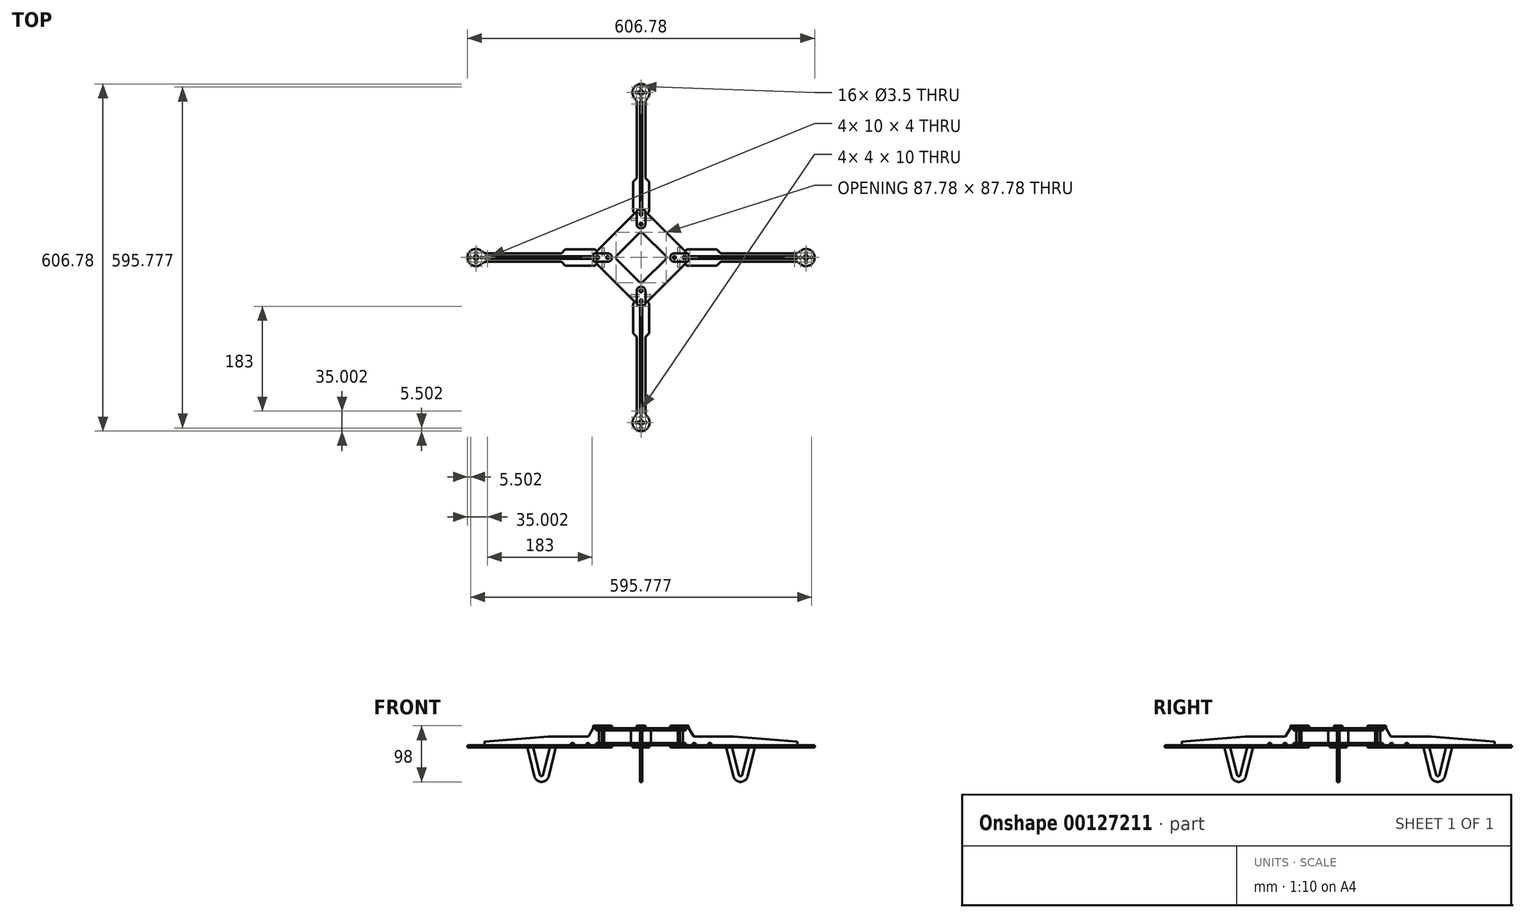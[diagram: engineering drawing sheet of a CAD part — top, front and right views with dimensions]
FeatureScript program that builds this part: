
annotation { "Feature Type Name" : "Feature", "Feature Type Description" : "" }
export const myFeature = defineFeature(function(context is Context, id is Id, definition is map)
    precondition{}
    {
        {
            assignVariable(context, id + "F0", {"name" : "Dicke", "anyValue" : 4 * mm});
        }
        {
            var Q0;
            Q0=qCreatedBy(makeId("Right.planeOp"),FACE);
            var sketch = newSketch(context, id + "F1", { "sketchPlane" : qUnion([Q0])});
            skLineSegment(sketch, "E0", {"start": v(0, 0) * mm, "end": v(0, 100) * mm, "construction": true});
            skSolve(sketch);
        }
        {
            var Q0;
            Q0=qCreatedBy(makeId("Top.planeOp"),FACE);
            var sketch = newSketch(context, id + "F2", { "sketchPlane" : qUnion([Q0])});
            skLineSegment(sketch, "E1.bottom", {"start": v(10, 78.39) * mm, "end": v(2, 78.39) * mm});
            skLineSegment(sketch, "E1.top", {"start": v(10, -78.39) * mm, "end": v(2, -78.39) * mm});
            skLineSegment(sketch, "E1.left", {"start": v(78.39, 10) * mm, "end": v(78.39, 2) * mm});
            skLineSegment(sketch, "E1.right", {"start": v(-78.39, 10) * mm, "end": v(-78.39, 2) * mm});
            skPoint(sketch, "E1.middle", {"position": v(0, 0) * mm});
            skLineSegment(sketch, "E2", {"start": v(-2, -78.39) * mm, "end": v(-2, -73.39) * mm});
            skLineSegment(sketch, "E3", {"start": v(-2, -73.39) * mm, "end": v(2, -73.39) * mm});
            skLineSegment(sketch, "E4", {"start": v(2, -73.39) * mm, "end": v(2, -78.39) * mm});
            skLineSegment(sketch, "E5", {"start": v(-78.39, -2) * mm, "end": v(-73.39, -2) * mm});
            skLineSegment(sketch, "E6", {"start": v(-73.39, -2) * mm, "end": v(-73.39, 2) * mm});
            skLineSegment(sketch, "E7", {"start": v(-73.39, 2) * mm, "end": v(-78.39, 2) * mm});
            skLineSegment(sketch, "E8.MirrorCS", {"start": v(-2, 73.39) * mm, "end": v(2, 73.39) * mm});
            skLineSegment(sketch, "E9.MirrorCS", {"start": v(-2, 78.39) * mm, "end": v(-2, 73.39) * mm});
            skLineSegment(sketch, "E10.MirrorCS", {"start": v(2, 73.39) * mm, "end": v(2, 78.39) * mm});
            skLineSegment(sketch, "E11.MirrorCS", {"start": v(73.39, -2) * mm, "end": v(73.39, 2) * mm});
            skLineSegment(sketch, "E12.MirrorCS", {"start": v(78.39, -2) * mm, "end": v(73.39, -2) * mm});
            skLineSegment(sketch, "E13.MirrorCS", {"start": v(73.39, 2) * mm, "end": v(78.39, 2) * mm});
            skLineSegment(sketch, "E14.trimOffspring", {"start": v(-2, -78.39) * mm, "end": v(-10, -78.39) * mm});
            skLineSegment(sketch, "E15.trimOffspring", {"start": v(-78.39, -2) * mm, "end": v(-78.39, -10) * mm});
            skLineSegment(sketch, "E16.trimOffspring", {"start": v(78.39, -2) * mm, "end": v(78.39, -10) * mm});
            skLineSegment(sketch, "E17.trimOffspring", {"start": v(-2, 78.39) * mm, "end": v(-10, 78.39) * mm});
            skLineSegment(sketch, "E18", {"start": v(-78.39, 10) * mm, "end": v(-10, 78.39) * mm});
            skPoint(sketch, "E19.orphan", {"position": v(-78.39, 78.39) * mm});
            skLineSegment(sketch, "E20.MirrorCS", {"start": v(78.39, 10) * mm, "end": v(10, 78.39) * mm});
            skLineSegment(sketch, "E21.MirrorCS", {"start": v(78.39, -10) * mm, "end": v(10, -78.39) * mm});
            skLineSegment(sketch, "E22.MirrorCS", {"start": v(-78.39, -10) * mm, "end": v(-10, -78.39) * mm});
            skPoint(sketch, "E23.orphan", {"position": v(-78.39, -78.39) * mm});
            skPoint(sketch, "E24.orphan", {"position": v(78.39, -78.39) * mm});
            skPoint(sketch, "E25.orphan", {"position": v(78.39, 78.39) * mm});
            skSolve(sketch);
        }
        {
            var Q0;
            Q0 = qSketchRegion(id + "F2", true);
            extrude(context, id + "F3", {"entities" : qUnion([Q0]), "depth" : getVariable(context, 'Dicke')});
        }
        {
            var Q0;
            Q0=qCreatedBy(makeId("Top.planeOp"),FACE);
            cPlane(context, id + "F4", {"entities" : qUnion([Q0]), "cplaneType" : CPlaneType.OFFSET, "offset" : 30 * mm, "width" : 150 * mm, "height" : 150 * mm});
        }
        {
            var Q0;
            Q0=makeQuery(id+"F3.opExtrude","SWEPT_BODY",BODY,{"disambiguationData":[OSD([sQuery(id+"F2.wireOp",EDGE,"E1.bottom"),sQuery(id+"F2.wireOp",EDGE,"E1.top"),sQuery(id+"F2.wireOp",EDGE,"E1.left"),sQuery(id+"F2.wireOp",EDGE,"E1.right"),sQuery(id+"F2.wireOp",EDGE,"E2"),sQuery(id+"F2.wireOp",EDGE,"E3"),sQuery(id+"F2.wireOp",EDGE,"E4"),sQuery(id+"F2.wireOp",EDGE,"E5"),sQuery(id+"F2.wireOp",EDGE,"E6"),sQuery(id+"F2.wireOp",EDGE,"E7"),sQuery(id+"F2.wireOp",EDGE,"E8.MirrorCS"),sQuery(id+"F2.wireOp",EDGE,"E9.MirrorCS"),sQuery(id+"F2.wireOp",EDGE,"E10.MirrorCS"),sQuery(id+"F2.wireOp",EDGE,"E11.MirrorCS"),sQuery(id+"F2.wireOp",EDGE,"E12.MirrorCS"),sQuery(id+"F2.wireOp",EDGE,"E13.MirrorCS"),sQuery(id+"F2.wireOp",EDGE,"E14.trimOffspring"),sQuery(id+"F2.wireOp",EDGE,"E15.trimOffspring"),sQuery(id+"F2.wireOp",EDGE,"E16.trimOffspring"),sQuery(id+"F2.wireOp",EDGE,"E17.trimOffspring"),sQuery(id+"F2.wireOp",EDGE,"E18"),sQuery(id+"F2.wireOp",EDGE,"E20.MirrorCS"),sQuery(id+"F2.wireOp",EDGE,"E21.MirrorCS"),sQuery(id+"F2.wireOp",EDGE,"E22.MirrorCS")])]});
            transform(context, id + "F5", {"entities" : qUnion([Q0]), "transformType" : TransformType.TRANSLATION_3D, "dx" : 0 * mm, "dy" : 0 * mm, "dz" : 26 * mm, "makeCopy" : true});
        }
        {
            var Q0;
            Q0=makeQuery(id+"F5.opPattern","COPY",FACE,{"derivedFrom":makeQuery(id+"F3.opExtrude","CAP_FACE",FACE,{"disambiguationData":[OSD([sQuery(id+"F2.wireOp",EDGE,"E1.bottom"),sQuery(id+"F2.wireOp",EDGE,"E1.top"),sQuery(id+"F2.wireOp",EDGE,"E1.left"),sQuery(id+"F2.wireOp",EDGE,"E1.right"),sQuery(id+"F2.wireOp",EDGE,"E2"),sQuery(id+"F2.wireOp",EDGE,"E3"),sQuery(id+"F2.wireOp",EDGE,"E4"),sQuery(id+"F2.wireOp",EDGE,"E5"),sQuery(id+"F2.wireOp",EDGE,"E6"),sQuery(id+"F2.wireOp",EDGE,"E7"),sQuery(id+"F2.wireOp",EDGE,"E8.MirrorCS"),sQuery(id+"F2.wireOp",EDGE,"E9.MirrorCS"),sQuery(id+"F2.wireOp",EDGE,"E10.MirrorCS"),sQuery(id+"F2.wireOp",EDGE,"E11.MirrorCS"),sQuery(id+"F2.wireOp",EDGE,"E12.MirrorCS"),sQuery(id+"F2.wireOp",EDGE,"E13.MirrorCS"),sQuery(id+"F2.wireOp",EDGE,"E14.trimOffspring"),sQuery(id+"F2.wireOp",EDGE,"E15.trimOffspring"),sQuery(id+"F2.wireOp",EDGE,"E16.trimOffspring"),sQuery(id+"F2.wireOp",EDGE,"E17.trimOffspring"),sQuery(id+"F2.wireOp",EDGE,"E18"),sQuery(id+"F2.wireOp",EDGE,"E20.MirrorCS"),sQuery(id+"F2.wireOp",EDGE,"E21.MirrorCS"),sQuery(id+"F2.wireOp",EDGE,"E22.MirrorCS")])],"isStart":false}),"instanceName":"1"});
            var sketch = newSketch(context, id + "F6", { "sketchPlane" : qUnion([Q0])});
            skLineSegment(sketch, "E26", {"start": v(0, -45.96) * mm, "end": v(45.96, 0) * mm});
            skLineSegment(sketch, "E27", {"start": v(45.96, 0) * mm, "end": v(0, 45.96) * mm});
            skLineSegment(sketch, "E28", {"start": v(0, 45.96) * mm, "end": v(-45.96, 0) * mm});
            skLineSegment(sketch, "E29", {"start": v(-45.96, 0) * mm, "end": v(0, -45.96) * mm});
            skSolve(sketch);
        }
        {
            var Q0;
            Q0 = qSketchRegion(id + "F6", true);
            extrude(context, id + "F7", {"entities" : qUnion([Q0]), "operationType" : NewBodyOperationType.REMOVE, "oppositeDirection" : true, "depth" : 25 * mm});
        }
        {
            var Q0;
            Q0=makeQuery(id+"F7.boolean.opBoolean","COPY",EDGE,{"derivedFrom":makeQuery(id+"F7.opExtrude","SWEPT_EDGE",EDGE,{"disambiguationData":[OSD([sQuery(id+"F6.wireOp",EDGE,"E26"),sQuery(id+"F6.wireOp",EDGE,"E29")])]})});
            var Q1;
            Q1=makeQuery(id+"F7.boolean.opBoolean","COPY",EDGE,{"derivedFrom":makeQuery(id+"F7.opExtrude","SWEPT_EDGE",EDGE,{"disambiguationData":[OSD([sQuery(id+"F6.wireOp",EDGE,"E28"),sQuery(id+"F6.wireOp",EDGE,"E29")])]})});
            var Q2;
            Q2=makeQuery(id+"F7.boolean.opBoolean","COPY",EDGE,{"derivedFrom":makeQuery(id+"F7.opExtrude","SWEPT_EDGE",EDGE,{"disambiguationData":[OSD([sQuery(id+"F6.wireOp",EDGE,"E27"),sQuery(id+"F6.wireOp",EDGE,"E28")])]})});
            var Q3;
            Q3=makeQuery(id+"F7.boolean.opBoolean","COPY",EDGE,{"derivedFrom":makeQuery(id+"F7.opExtrude","SWEPT_EDGE",EDGE,{"disambiguationData":[OSD([sQuery(id+"F6.wireOp",EDGE,"E26"),sQuery(id+"F6.wireOp",EDGE,"E27")])]})});
            fillet(context, id + "F8", {"entities" : qUnion([Q0, Q1, Q2, Q3]), "radius" : 5 * mm, "tangentPropagation" : true, "allowEdgeOverflow" : false});
        }
        {
            var Q0;
            Q0=qCreatedBy(makeId("Top.planeOp"),FACE);
            var sketch = newSketch(context, id + "F9", { "sketchPlane" : qUnion([Q0])});
            skArc(sketch, "E30", {"start": v(10.5, 277.68) * mm, "mid": v(0, 303.39) * mm, "end": v(-10.5, 277.68) * mm});
            skLineSegment(sketch, "E31", {"start": v(-7.5, 270.53) * mm, "end": v(-7.5, 138.89) * mm});
            skArc(sketch, "E32", {"start": v(-7.5, 58.39) * mm, "mid": v(0, 50.89) * mm, "end": v(7.5, 58.39) * mm});
            skLineSegment(sketch, "E33", {"start": v(7.5, 58.39) * mm, "end": v(7.5, 73.89) * mm});
            skPoint(sketch, "E34.visualSharp", {"position": v(7.5, 275.4) * mm});
            skArc(sketch, "E34.filletArc", {"start": v(10.5, 277.68) * mm, "mid": v(8.28, 274.4) * mm, "end": v(7.5, 270.53) * mm});
            skPoint(sketch, "E35.visualSharp", {"position": v(-7.5, 275.4) * mm});
            skArc(sketch, "E35.filletArc", {"start": v(-7.5, 270.53) * mm, "mid": v(-8.28, 274.4) * mm, "end": v(-10.5, 277.68) * mm});
            skPoint(sketch, "E36", {"position": v(0, 303.39) * mm});
            skLineSegment(sketch, "E37", {"start": v(0, 278.89) * mm, "end": v(0, 297.89) * mm, "construction": true});
            skLineSegment(sketch, "E38", {"start": v(-8, 288.39) * mm, "end": v(8, 288.39) * mm, "construction": true});
            skCircle(sketch, "E39", {"center": v(-8, 288.39) * mm, "radius": 1.75 * mm});
            skCircle(sketch, "E40", {"center": v(0, 297.89) * mm, "radius": 1.75 * mm});
            skCircle(sketch, "E41", {"center": v(8, 288.39) * mm, "radius": 1.75 * mm});
            skCircle(sketch, "E42", {"center": v(0, 278.89) * mm, "radius": 1.75 * mm});
            skCircle(sketch, "E43", {"center": v(0, 58.39) * mm, "radius": 2.5 * mm});
            skLineSegment(sketch, "E44", {"start": v(7.5, 73.89) * mm, "end": v(14, 80.39) * mm});
            skLineSegment(sketch, "E45", {"start": v(14, 80.39) * mm, "end": v(14, 132.39) * mm});
            skLineSegment(sketch, "E46", {"start": v(14, 132.39) * mm, "end": v(7.5, 138.89) * mm});
            skLineSegment(sketch, "E47.MirrorCS", {"start": v(-7.5, 73.89) * mm, "end": v(-14, 80.39) * mm});
            skLineSegment(sketch, "E48.MirrorCS", {"start": v(-14, 80.39) * mm, "end": v(-14, 132.39) * mm});
            skLineSegment(sketch, "E49.MirrorCS", {"start": v(-14, 132.39) * mm, "end": v(-7.5, 138.89) * mm});
            skLineSegment(sketch, "E50.trimOffspring", {"start": v(7.5, 138.89) * mm, "end": v(7.5, 270.53) * mm});
            skLineSegment(sketch, "E51.trimOffspring", {"start": v(-7.5, 73.89) * mm, "end": v(-7.5, 58.39) * mm});
            skLineSegment(sketch, "E52", {"start": v(7.5, 73.89) * mm, "end": v(-7.5, 73.89) * mm, "construction": true});
            skCircle(sketch, "E53", {"center": v(0, 288.39) * mm, "radius": 4 * mm});
            skSolve(sketch);
        }
        {
            var Q0;
            Q0=qCreatedBy(makeId("Top.planeOp"),FACE);
            var sketch = newSketch(context, id + "F10", { "sketchPlane" : qUnion([Q0])});
            skCircle(sketch, "E54", {"center": v(0, 288.39) * mm, "radius": 14 * mm});
            skCircle(sketch, "E55", {"center": v(0, 288.39) * mm, "radius": 127 * mm});
            skSolve(sketch);
        }
        {
            var Q0;
            Q0 = qSketchRegion(id + "F9", true);
            extrude(context, id + "F11", {"entities" : qUnion([Q0]), "oppositeDirection" : true, "depth" : getVariable(context, 'Dicke')});
        }
        {
            var Q0;
            Q0=qCreatedBy(makeId("Right.planeOp"),FACE);
            var sketch = newSketch(context, id + "F12", { "sketchPlane" : qUnion([Q0])});
            skLineSegment(sketch, "E56", {"start": v(92.05, 15) * mm, "end": v(162.05, 15) * mm});
            skLineSegment(sketch, "E57", {"start": v(162.05, 15) * mm, "end": v(273.39, 6) * mm});
            skLineSegment(sketch, "E58", {"start": v(273.39, 6) * mm, "end": v(273.39, -4) * mm});
            skLineSegment(sketch, "E59", {"start": v(263.39, 0) * mm, "end": v(122.39, 0) * mm});
            skLineSegment(sketch, "E60", {"start": v(73.39, 0) * mm, "end": v(73.39, 34) * mm});
            skLineSegment(sketch, "E61.top", {"start": v(90.39, 4) * mm, "end": v(95.39, 4) * mm});
            skLineSegment(sketch, "E61.left", {"start": v(90.39, -4) * mm, "end": v(90.39, 4) * mm});
            skLineSegment(sketch, "E61.right", {"start": v(95.39, 0) * mm, "end": v(95.39, 4) * mm});
            skLineSegment(sketch, "E62.top", {"start": v(122.39, 4) * mm, "end": v(117.39, 4) * mm});
            skLineSegment(sketch, "E62.left", {"start": v(122.39, 0) * mm, "end": v(122.39, 4) * mm});
            skLineSegment(sketch, "E62.right", {"start": v(117.39, 0) * mm, "end": v(117.39, 4) * mm});
            skLineSegment(sketch, "E63.trimOffspring", {"start": v(80.39, 0) * mm, "end": v(73.39, 0) * mm});
            skLineSegment(sketch, "E64.trimOffspring", {"start": v(117.39, 0) * mm, "end": v(95.39, 0) * mm});
            skLineSegment(sketch, "E65", {"start": v(92.05, 15) * mm, "end": v(83.39, 30) * mm});
            skLineSegment(sketch, "E66", {"start": v(83.39, 30) * mm, "end": v(78.39, 30) * mm});
            skLineSegment(sketch, "E67", {"start": v(78.39, 30) * mm, "end": v(78.39, 34) * mm});
            skLineSegment(sketch, "E68", {"start": v(78.39, 34) * mm, "end": v(73.39, 34) * mm});
            skLineSegment(sketch, "E69", {"start": v(80.39, 0) * mm, "end": v(80.39, -4) * mm});
            skLineSegment(sketch, "E70", {"start": v(80.39, -4) * mm, "end": v(90.39, -4) * mm});
            skLineSegment(sketch, "E71", {"start": v(263.39, 0) * mm, "end": v(263.39, -4) * mm});
            skLineSegment(sketch, "E72", {"start": v(263.39, -4) * mm, "end": v(273.39, -4) * mm});
            skSolve(sketch);
        }
        {
            var Q0;
            Q0 = qSketchRegion(id + "F12", true);
            extrude(context, id + "F13", {"entities" : qUnion([Q0]), "endBound" : BoundingType.SYMMETRIC, "depth" : getVariable(context, 'Dicke')});
        }
        {
            var Q0;
            Q0=qCreatedBy(makeId("Right.planeOp"),FACE);
            var sketch = newSketch(context, id + "F14", { "sketchPlane" : qUnion([Q0])});
            skLineSegment(sketch, "E73", {"start": v(148.89, -4) * mm, "end": v(161.27, -54.12) * mm});
            skArc(sketch, "E74", {"start": v(161.27, -54.12) * mm, "mid": v(173.89, -64) * mm, "end": v(186.5, -54.12) * mm});
            skLineSegment(sketch, "E75", {"start": v(186.5, -54.12) * mm, "end": v(198.89, -4) * mm});
            skLineSegment(sketch, "E76.0", {"start": v(176.8, -51.72) * mm, "end": v(188.59, -4) * mm});
            skArc(sketch, "E76.1", {"start": v(170.98, -51.72) * mm, "mid": v(173.89, -54) * mm, "end": v(176.8, -51.72) * mm});
            skLineSegment(sketch, "E76.2", {"start": v(159.19, -4) * mm, "end": v(170.98, -51.72) * mm});
            skLineSegment(sketch, "E77", {"start": v(148.89, -4) * mm, "end": v(154.19, -4) * mm});
            skLineSegment(sketch, "E78", {"start": v(154.19, -4) * mm, "end": v(154.19, 0) * mm});
            skLineSegment(sketch, "E79", {"start": v(154.19, 0) * mm, "end": v(159.19, 0) * mm});
            skLineSegment(sketch, "E80", {"start": v(159.19, 0) * mm, "end": v(159.19, -4) * mm});
            skLineSegment(sketch, "E81", {"start": v(188.59, -4) * mm, "end": v(188.59, 0) * mm});
            skLineSegment(sketch, "E82", {"start": v(188.59, 0) * mm, "end": v(193.59, 0) * mm});
            skLineSegment(sketch, "E83", {"start": v(193.59, 0) * mm, "end": v(193.59, -4) * mm});
            skLineSegment(sketch, "E84", {"start": v(193.59, -4) * mm, "end": v(198.89, -4) * mm});
            skSolve(sketch);
        }
        {
            var Q0;
            Q0 = qSketchRegion(id + "F14", true);
            extrude(context, id + "F15", {"entities" : qUnion([Q0]), "endBound" : BoundingType.SYMMETRIC, "depth" : getVariable(context, 'Dicke')});
        }
        {
            var Q0;
            Q0=qCreatedBy(id+"F4.planeOp",FACE);
            var sketch = newSketch(context, id + "F16", { "sketchPlane" : qUnion([Q0])});
            skLineSegment(sketch, "E85.0", {"start": v(-7.5, 73.89) * mm, "end": v(-7.5, 58.39) * mm});
            skArc(sketch, "E86.0", {"start": v(-7.5, 58.39) * mm, "mid": v(0, 50.89) * mm, "end": v(7.5, 58.39) * mm});
            skLineSegment(sketch, "E87.0", {"start": v(7.5, 58.39) * mm, "end": v(7.5, 73.89) * mm});
            skCircle(sketch, "E88.0", {"center": v(0, 58.39) * mm, "radius": 2.5 * mm});
            skLineSegment(sketch, "E89", {"start": v(-7.5, 73.89) * mm, "end": v(-7.5, 80.39) * mm});
            skLineSegment(sketch, "E90", {"start": v(7.5, 73.89) * mm, "end": v(7.5, 80.39) * mm});
            skLineSegment(sketch, "E91", {"start": v(-4.5, 83.39) * mm, "end": v(4.5, 83.39) * mm});
            skPoint(sketch, "E92.visualSharp", {"position": v(-7.5, 83.39) * mm});
            skArc(sketch, "E92.filletArc", {"start": v(-4.5, 83.39) * mm, "mid": v(-6.62, 82.5) * mm, "end": v(-7.5, 80.39) * mm});
            skPoint(sketch, "E93.visualSharp", {"position": v(7.5, 83.39) * mm});
            skArc(sketch, "E93.filletArc", {"start": v(7.5, 80.39) * mm, "mid": v(6.62, 82.5) * mm, "end": v(4.5, 83.39) * mm});
            skSolve(sketch);
        }
        {
            var Q0;
            Q0 = qSketchRegion(id + "F16", true);
            extrude(context, id + "F17", {"entities" : qUnion([Q0]), "depth" : getVariable(context, 'Dicke')});
        }
        {
            var Q0;
            Q0=makeQuery(id+"F13.opExtrude","SWEPT_BODY",BODY,{"disambiguationData":[OSD([sQuery(id+"F12.wireOp",EDGE,"E56"),sQuery(id+"F12.wireOp",EDGE,"E57"),sQuery(id+"F12.wireOp",EDGE,"E58"),sQuery(id+"F12.wireOp",EDGE,"E59"),sQuery(id+"F12.wireOp",EDGE,"E60"),sQuery(id+"F12.wireOp",EDGE,"E61.top"),sQuery(id+"F12.wireOp",EDGE,"E61.left"),sQuery(id+"F12.wireOp",EDGE,"E61.right"),sQuery(id+"F12.wireOp",EDGE,"E62.top"),sQuery(id+"F12.wireOp",EDGE,"E62.left"),sQuery(id+"F12.wireOp",EDGE,"E62.right"),sQuery(id+"F12.wireOp",EDGE,"E63.trimOffspring"),sQuery(id+"F12.wireOp",EDGE,"E64.trimOffspring"),sQuery(id+"F12.wireOp",EDGE,"E65"),sQuery(id+"F12.wireOp",EDGE,"E66"),sQuery(id+"F12.wireOp",EDGE,"E67"),sQuery(id+"F12.wireOp",EDGE,"E68")])]});
            var Q1;
            Q1=makeQuery(id+"F17.opExtrude","SWEPT_BODY",BODY,{"disambiguationData":[OSD([sQuery(id+"F16.wireOp",EDGE,"E85.0"),sQuery(id+"F16.wireOp",EDGE,"E86.0"),sQuery(id+"F16.wireOp",EDGE,"E87.0"),sQuery(id+"F16.wireOp",EDGE,"E88.0"),sQuery(id+"F16.wireOp",EDGE,"E89"),sQuery(id+"F16.wireOp",EDGE,"E90"),sQuery(id+"F16.wireOp",EDGE,"E91"),sQuery(id+"F16.wireOp",EDGE,"E92.filletArc"),sQuery(id+"F16.wireOp",EDGE,"E93.filletArc")])]});
            var Q2;
            Q2=makeQuery(id+"F3.opExtrude","SWEPT_BODY",BODY,{"disambiguationData":[OSD([sQuery(id+"F2.wireOp",EDGE,"E1.bottom"),sQuery(id+"F2.wireOp",EDGE,"E1.top"),sQuery(id+"F2.wireOp",EDGE,"E1.left"),sQuery(id+"F2.wireOp",EDGE,"E1.right")])]});
            var Q3;
            Q3=makeQuery(id+"FhrMNaqe6fnIL6q_1.opExtrude","SWEPT_BODY",BODY,{"disambiguationData":[OSD([sQuery(id+"FcWjo9COieUKBjw_1.wireOp",EDGE,"a90fca38-8a13-4d0b-956b-f1cffcdc3152.0"),sQuery(id+"FcWjo9COieUKBjw_1.wireOp",EDGE,"fbc8aa7a-db77-4349-b2f0-69285a5e3160.0"),sQuery(id+"FcWjo9COieUKBjw_1.wireOp",EDGE,"03366df2-630f-4610-a856-3e1fcb18efef.0"),sQuery(id+"FcWjo9COieUKBjw_1.wireOp",EDGE,"1a7c9859-e6ac-4236-bc2e-86e582c79c75.0"),sQuery(id+"FcWjo9COieUKBjw_1.wireOp",EDGE,"497b7f40-1a27-446f-bee7-4e00cf973d28.0"),sQuery(id+"FcWjo9COieUKBjw_1.wireOp",EDGE,"497b7f40-1a27-446f-bee7-4e00cf973d28.1"),sQuery(id+"FcWjo9COieUKBjw_1.wireOp",EDGE,"497b7f40-1a27-446f-bee7-4e00cf973d28.2"),sQuery(id+"FcWjo9COieUKBjw_1.wireOp",EDGE,"497b7f40-1a27-446f-bee7-4e00cf973d28.3")])]});
            booleanBodies(context, id + "F18", {"operationType" : BooleanOperationType.SUBTRACTION, "tools" : qUnion([Q0]), "targets" : qUnion([Q1, Q2, Q3]), "keepTools" : true});
        }
        {
            var Q0;
            Q0=makeQuery(id+"F13.opExtrude","SWEPT_BODY",BODY,{"disambiguationData":[OSD([sQuery(id+"F12.wireOp",EDGE,"E56"),sQuery(id+"F12.wireOp",EDGE,"E57"),sQuery(id+"F12.wireOp",EDGE,"E58"),sQuery(id+"F12.wireOp",EDGE,"E59"),sQuery(id+"F12.wireOp",EDGE,"E60"),sQuery(id+"F12.wireOp",EDGE,"E61.top"),sQuery(id+"F12.wireOp",EDGE,"E61.left"),sQuery(id+"F12.wireOp",EDGE,"E61.right"),sQuery(id+"F12.wireOp",EDGE,"E62.top"),sQuery(id+"F12.wireOp",EDGE,"E62.left"),sQuery(id+"F12.wireOp",EDGE,"E62.right"),sQuery(id+"F12.wireOp",EDGE,"E63.trimOffspring"),sQuery(id+"F12.wireOp",EDGE,"E64.trimOffspring"),sQuery(id+"F12.wireOp",EDGE,"E65"),sQuery(id+"F12.wireOp",EDGE,"E66"),sQuery(id+"F12.wireOp",EDGE,"E67"),sQuery(id+"F12.wireOp",EDGE,"E68"),sQuery(id+"F12.wireOp",EDGE,"E69"),sQuery(id+"F12.wireOp",EDGE,"E70"),sQuery(id+"F12.wireOp",EDGE,"E71"),sQuery(id+"F12.wireOp",EDGE,"E72")])]});
            var Q1;
            Q1=makeQuery(id+"F15.opExtrude","SWEPT_BODY",BODY,{"disambiguationData":[OSD([sQuery(id+"F14.wireOp",EDGE,"E73"),sQuery(id+"F14.wireOp",EDGE,"E74"),sQuery(id+"F14.wireOp",EDGE,"E75"),sQuery(id+"F14.wireOp",EDGE,"E76.0"),sQuery(id+"F14.wireOp",EDGE,"E76.1"),sQuery(id+"F14.wireOp",EDGE,"E76.2"),sQuery(id+"F14.wireOp",EDGE,"E77"),sQuery(id+"F14.wireOp",EDGE,"E78"),sQuery(id+"F14.wireOp",EDGE,"E79"),sQuery(id+"F14.wireOp",EDGE,"E80"),sQuery(id+"F14.wireOp",EDGE,"E81"),sQuery(id+"F14.wireOp",EDGE,"E82"),sQuery(id+"F14.wireOp",EDGE,"E83"),sQuery(id+"F14.wireOp",EDGE,"E84")])]});
            var Q2;
            Q2=makeQuery(id+"F11.opExtrude","SWEPT_BODY",BODY,{"disambiguationData":[OSD([sQuery(id+"F9.wireOp",EDGE,"E30"),sQuery(id+"F9.wireOp",EDGE,"E31"),sQuery(id+"F9.wireOp",EDGE,"E32"),sQuery(id+"F9.wireOp",EDGE,"E33"),sQuery(id+"F9.wireOp",EDGE,"E34.filletArc"),sQuery(id+"F9.wireOp",EDGE,"E35.filletArc"),sQuery(id+"F9.wireOp",EDGE,"E39"),sQuery(id+"F9.wireOp",EDGE,"E40"),sQuery(id+"F9.wireOp",EDGE,"E41"),sQuery(id+"F9.wireOp",EDGE,"E42"),sQuery(id+"F9.wireOp",EDGE,"E43"),sQuery(id+"F9.wireOp",EDGE,"E44"),sQuery(id+"F9.wireOp",EDGE,"E45"),sQuery(id+"F9.wireOp",EDGE,"E46"),sQuery(id+"F9.wireOp",EDGE,"E47.MirrorCS"),sQuery(id+"F9.wireOp",EDGE,"E48.MirrorCS"),sQuery(id+"F9.wireOp",EDGE,"E49.MirrorCS"),sQuery(id+"F9.wireOp",EDGE,"E50.trimOffspring"),sQuery(id+"F9.wireOp",EDGE,"E51.trimOffspring")])]});
            booleanBodies(context, id + "F19", {"operationType" : BooleanOperationType.SUBTRACTION, "tools" : qUnion([Q0, Q1]), "targets" : qUnion([Q2]), "keepTools" : true});
        }
        {
            var Q0;
            Q0=makeQuery(id+"F3.opExtrude","CAP_FACE",FACE,{"disambiguationData":[OSD([sQuery(id+"F2.wireOp",EDGE,"E1.bottom"),sQuery(id+"F2.wireOp",EDGE,"E1.top"),sQuery(id+"F2.wireOp",EDGE,"E1.left"),sQuery(id+"F2.wireOp",EDGE,"E1.right"),sQuery(id+"F2.wireOp",EDGE,"E2"),sQuery(id+"F2.wireOp",EDGE,"E3"),sQuery(id+"F2.wireOp",EDGE,"E4"),sQuery(id+"F2.wireOp",EDGE,"E5"),sQuery(id+"F2.wireOp",EDGE,"E6"),sQuery(id+"F2.wireOp",EDGE,"E7"),sQuery(id+"F2.wireOp",EDGE,"E8.MirrorCS"),sQuery(id+"F2.wireOp",EDGE,"E9.MirrorCS"),sQuery(id+"F2.wireOp",EDGE,"E10.MirrorCS"),sQuery(id+"F2.wireOp",EDGE,"E11.MirrorCS"),sQuery(id+"F2.wireOp",EDGE,"E12.MirrorCS"),sQuery(id+"F2.wireOp",EDGE,"E13.MirrorCS"),sQuery(id+"F2.wireOp",EDGE,"E14.trimOffspring"),sQuery(id+"F2.wireOp",EDGE,"E15.trimOffspring"),sQuery(id+"F2.wireOp",EDGE,"E16.trimOffspring"),sQuery(id+"F2.wireOp",EDGE,"E17.trimOffspring"),sQuery(id+"F2.wireOp",EDGE,"E18"),sQuery(id+"F2.wireOp",EDGE,"E20.MirrorCS"),sQuery(id+"F2.wireOp",EDGE,"E21.MirrorCS"),sQuery(id+"F2.wireOp",EDGE,"E22.MirrorCS")])],"isStart":false});
            var sketch = newSketch(context, id + "F20", { "sketchPlane" : qUnion([Q0])});
            skLineSegment(sketch, "E94.bottom", {"start": v(17.5, 68.39) * mm, "end": v(-17.5, 68.39) * mm});
            skLineSegment(sketch, "E94.top", {"start": v(17.5, 64.39) * mm, "end": v(-17.5, 64.39) * mm});
            skLineSegment(sketch, "E94.left", {"start": v(17.5, 68.39) * mm, "end": v(17.5, 64.39) * mm});
            skLineSegment(sketch, "E94.right", {"start": v(-17.5, 68.39) * mm, "end": v(-17.5, 64.39) * mm});
            skSolve(sketch);
        }
        {
            var Q0;
            Q0 = qSketchRegion(id + "F20", true);
            extrude(context, id + "F21", {"entities" : qUnion([Q0]), "endBound" : BoundingType.UP_TO_NEXT, "depth" : 25 * mm});
        }
        {
            var Q0;
            Q0=makeQuery(id+"F17.opExtrude","SWEPT_BODY",BODY,{"disambiguationData":[OSD([sQuery(id+"F16.wireOp",EDGE,"E85.0"),sQuery(id+"F16.wireOp",EDGE,"E86.0"),sQuery(id+"F16.wireOp",EDGE,"E87.0"),sQuery(id+"F16.wireOp",EDGE,"E88.0"),sQuery(id+"F16.wireOp",EDGE,"E89"),sQuery(id+"F16.wireOp",EDGE,"E90"),sQuery(id+"F16.wireOp",EDGE,"E91"),sQuery(id+"F16.wireOp",EDGE,"E92.filletArc"),sQuery(id+"F16.wireOp",EDGE,"E93.filletArc")])]});
            var Q1;
            Q1=makeQuery(id+"F15.opExtrude","SWEPT_BODY",BODY,{"disambiguationData":[OSD([sQuery(id+"F14.wireOp",EDGE,"E73"),sQuery(id+"F14.wireOp",EDGE,"E74"),sQuery(id+"F14.wireOp",EDGE,"E75"),sQuery(id+"F14.wireOp",EDGE,"E76.0"),sQuery(id+"F14.wireOp",EDGE,"E76.1"),sQuery(id+"F14.wireOp",EDGE,"E76.2"),sQuery(id+"F14.wireOp",EDGE,"E77"),sQuery(id+"F14.wireOp",EDGE,"E78"),sQuery(id+"F14.wireOp",EDGE,"E79"),sQuery(id+"F14.wireOp",EDGE,"E80"),sQuery(id+"F14.wireOp",EDGE,"E81"),sQuery(id+"F14.wireOp",EDGE,"E82"),sQuery(id+"F14.wireOp",EDGE,"E83"),sQuery(id+"F14.wireOp",EDGE,"E84")])]});
            var Q2;
            Q2=makeQuery(id+"F13.opExtrude","SWEPT_BODY",BODY,{"disambiguationData":[OSD([sQuery(id+"F12.wireOp",EDGE,"E56"),sQuery(id+"F12.wireOp",EDGE,"E57"),sQuery(id+"F12.wireOp",EDGE,"E58"),sQuery(id+"F12.wireOp",EDGE,"E59"),sQuery(id+"F12.wireOp",EDGE,"E60"),sQuery(id+"F12.wireOp",EDGE,"E61.top"),sQuery(id+"F12.wireOp",EDGE,"E61.left"),sQuery(id+"F12.wireOp",EDGE,"E61.right"),sQuery(id+"F12.wireOp",EDGE,"E62.top"),sQuery(id+"F12.wireOp",EDGE,"E62.left"),sQuery(id+"F12.wireOp",EDGE,"E62.right"),sQuery(id+"F12.wireOp",EDGE,"E63.trimOffspring"),sQuery(id+"F12.wireOp",EDGE,"E64.trimOffspring"),sQuery(id+"F12.wireOp",EDGE,"E65"),sQuery(id+"F12.wireOp",EDGE,"E66"),sQuery(id+"F12.wireOp",EDGE,"E67"),sQuery(id+"F12.wireOp",EDGE,"E68"),sQuery(id+"F12.wireOp",EDGE,"E69"),sQuery(id+"F12.wireOp",EDGE,"E70"),sQuery(id+"F12.wireOp",EDGE,"E71"),sQuery(id+"F12.wireOp",EDGE,"E72")])]});
            var Q3;
            Q3=makeQuery(id+"F11.opExtrude","SWEPT_BODY",BODY,{"disambiguationData":[OSD([sQuery(id+"F9.wireOp",EDGE,"E30"),sQuery(id+"F9.wireOp",EDGE,"E31"),sQuery(id+"F9.wireOp",EDGE,"E32"),sQuery(id+"F9.wireOp",EDGE,"E33"),sQuery(id+"F9.wireOp",EDGE,"E34.filletArc"),sQuery(id+"F9.wireOp",EDGE,"E35.filletArc"),sQuery(id+"F9.wireOp",EDGE,"E39"),sQuery(id+"F9.wireOp",EDGE,"E40"),sQuery(id+"F9.wireOp",EDGE,"E41"),sQuery(id+"F9.wireOp",EDGE,"E42"),sQuery(id+"F9.wireOp",EDGE,"E43"),sQuery(id+"F9.wireOp",EDGE,"E44"),sQuery(id+"F9.wireOp",EDGE,"E45"),sQuery(id+"F9.wireOp",EDGE,"E46"),sQuery(id+"F9.wireOp",EDGE,"E47.MirrorCS"),sQuery(id+"F9.wireOp",EDGE,"E48.MirrorCS"),sQuery(id+"F9.wireOp",EDGE,"E49.MirrorCS"),sQuery(id+"F9.wireOp",EDGE,"E50.trimOffspring"),sQuery(id+"F9.wireOp",EDGE,"E51.trimOffspring"),sQuery(id+"F9.wireOp",EDGE,"E53")])]});
            var Q4;
            Q4=makeQuery(id+"F21.opExtrude","SWEPT_BODY",BODY,{"disambiguationData":[OSD([sQuery(id+"F20.wireOp",EDGE,"E94.bottom"),sQuery(id+"F20.wireOp",EDGE,"E94.top"),sQuery(id+"F20.wireOp",EDGE,"E94.left"),sQuery(id+"F20.wireOp",EDGE,"E94.right")])]});
            var Q5;
            Q5=sQuery(id+"F1.wireOp",EDGE,"E0");
            circularPattern(context, id + "F22", {"entities" : qUnion([Q0, Q1, Q2, Q3, Q4]), "axis" : qUnion([Q5]), "angle" : 360 * degree, "instanceCount" : 4, "equalSpace" : true});
        }
    });
